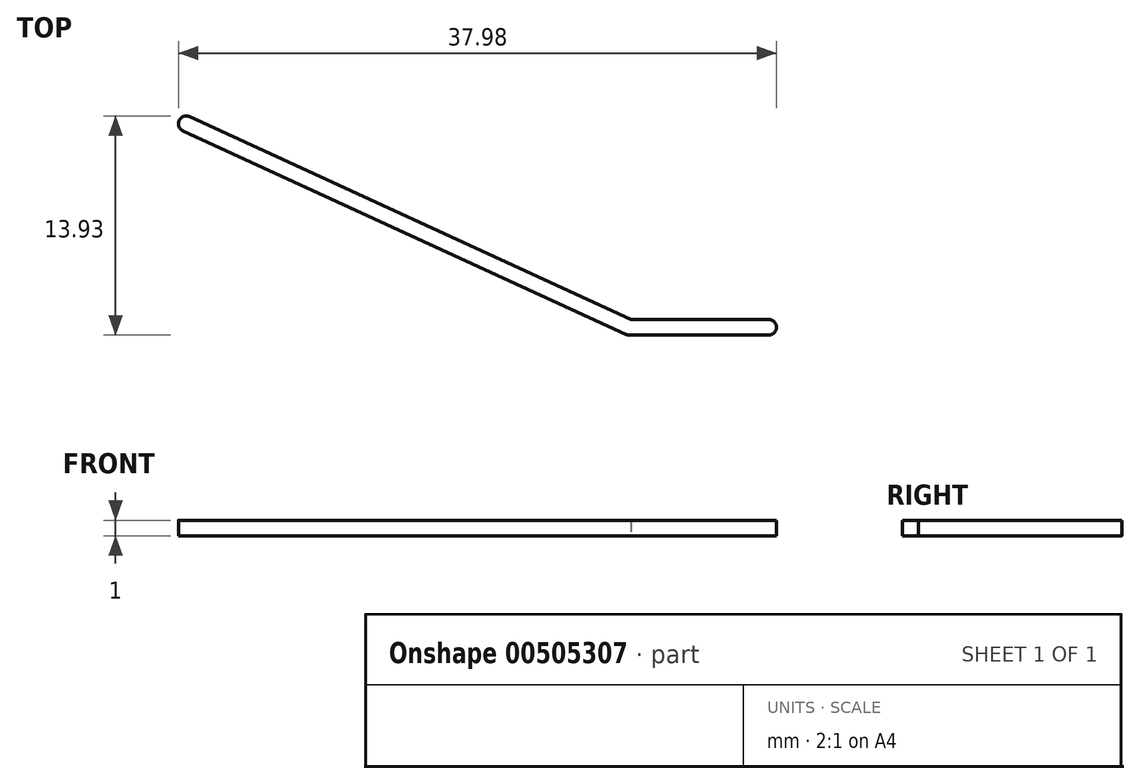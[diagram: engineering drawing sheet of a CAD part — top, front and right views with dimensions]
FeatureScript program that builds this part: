
annotation { "Feature Type Name" : "Feature", "Feature Type Description" : "" }
export const myFeature = defineFeature(function(context is Context, id is Id, definition is map)
    precondition{}
    {
        {
            var Q0;
            Q0=qCreatedBy(makeId("Top.planeOp"),FACE);
            var sketch = newSketch(context, id + "F0", { "sketchPlane" : qUnion([Q0])});
            skLineSegment(sketch, "E0", {"start": v(-63.48, 0) * mm, "end": v(0, 0) * mm});
            skLineSegment(sketch, "E1", {"start": v(0, 0) * mm, "end": v(28.14, -12.93) * mm});
            skLineSegment(sketch, "E2", {"start": v(28.14, -12.93) * mm, "end": v(36.98, -12.93) * mm});
            skLineSegment(sketch, "E3", {"start": v(36.98, -12.93) * mm, "end": v(75.6, 0) * mm});
            skArc(sketch, "E4.0.startCap", {"start": v(-63.48, -0.5) * mm, "mid": v(-63.98, 0) * mm, "end": v(-63.48, 0.5) * mm});
            skArc(sketch, "E4.0.endCap", {"start": v(0, 0.5) * mm, "mid": v(0.5, 0) * mm, "end": v(0, -0.5) * mm});
            skLineSegment(sketch, "E4.0.left", {"start": v(-63.48, 0.5) * mm, "end": v(0, 0.5) * mm});
            skLineSegment(sketch, "E4.0.right", {"start": v(-63.48, -0.5) * mm, "end": v(0, -0.5) * mm});
            skArc(sketch, "E4.1.startCap", {"start": v(-0.2, -0.45) * mm, "mid": v(-0.45, 0.2) * mm, "end": v(0.2, 0.45) * mm});
            skArc(sketch, "E4.1.endCap", {"start": v(28.35, -12.47) * mm, "mid": v(28.6, -13.13) * mm, "end": v(27.93, -13.38) * mm});
            skLineSegment(sketch, "E4.1.left", {"start": v(0.2, 0.45) * mm, "end": v(28.35, -12.47) * mm});
            skLineSegment(sketch, "E4.1.right", {"start": v(-0.2, -0.45) * mm, "end": v(27.93, -13.38) * mm});
            skArc(sketch, "E4.2.startCap", {"start": v(28.14, -13.43) * mm, "mid": v(27.64, -12.93) * mm, "end": v(28.14, -12.43) * mm});
            skArc(sketch, "E4.2.endCap", {"start": v(36.98, -12.43) * mm, "mid": v(37.48, -12.93) * mm, "end": v(36.98, -13.43) * mm});
            skLineSegment(sketch, "E4.2.left", {"start": v(28.14, -12.43) * mm, "end": v(36.98, -12.43) * mm});
            skLineSegment(sketch, "E4.2.right", {"start": v(28.14, -13.43) * mm, "end": v(36.98, -13.43) * mm});
            skArc(sketch, "E4.3.startCap", {"start": v(37.14, -13.4) * mm, "mid": v(36.5, -13.08) * mm, "end": v(36.82, -12.45) * mm});
            skArc(sketch, "E4.3.endCap", {"start": v(75.43, 0.47) * mm, "mid": v(76.07, 0.16) * mm, "end": v(75.75, -0.47) * mm});
            skLineSegment(sketch, "E4.3.left", {"start": v(36.82, -12.45) * mm, "end": v(75.43, 0.47) * mm});
            skLineSegment(sketch, "E4.3.right", {"start": v(37.14, -13.4) * mm, "end": v(75.75, -0.47) * mm});
            skSolve(sketch);
        }
        {
            var Q0;
            {var subQ5=sQuery(id+"F0.wireOp",EDGE,"E4.0.startCap");Q0=makeQuery(id+"F0.imprint","IMPRINT",FACE,{"disambiguationData":[TD([[makeQuery(id+"F0.imprint","IMPRINT",EDGE,{"derivedFrom":subQ5}),-1.0]])]});}
            var Q1;
            {var subQ3=sQuery(id+"F0.wireOp",EDGE,"E1");var subQ5=sQuery(id+"F0.wireOp",EDGE,"E0");var subQ6=makeQuery(id+"F0.imprint","INTERSECT",VERTEX,{"derivedFrom":[subQ5,subQ3]});Q1=makeQuery(id+"F0.imprint","IMPRINT",FACE,{"disambiguationData":[TD([[makeQuery(id+"F0.imprint","IMPRINT",EDGE,{"disambiguationData":[TD([[subQ6,1.0]])],"derivedFrom":subQ5}),1.0]])]});}
            var Q2;
            {var subQ5=sQuery(id+"F0.wireOp",EDGE,"E1");var subQ6=sQuery(id+"F0.wireOp",EDGE,"E0");var subQ7=makeQuery(id+"F0.imprint","INTERSECT",VERTEX,{"derivedFrom":[subQ6,subQ5]});Q2=makeQuery(id+"F0.imprint","IMPRINT",FACE,{"disambiguationData":[TD([[makeQuery(id+"F0.imprint","IMPRINT",EDGE,{"disambiguationData":[TD([[subQ7,1.0]])],"derivedFrom":subQ6}),-1.0]])]});}
            var Q3;
            {var subQ1=sQuery(id+"F0.wireOp",EDGE,"E4.0.endCap");var subQ5=sQuery(id+"F0.wireOp",EDGE,"E1");var subQ6=makeQuery(id+"F0.imprint","INTERSECT",VERTEX,{"derivedFrom":[subQ5,subQ1]});Q3=makeQuery(id+"F0.imprint","IMPRINT",FACE,{"disambiguationData":[TD([[makeQuery(id+"F0.imprint","IMPRINT",EDGE,{"disambiguationData":[TD([[subQ6,-1.0]])],"derivedFrom":subQ5}),-1.0]])]});}
            var Q4;
            {var subQ3=sQuery(id+"F0.wireOp",EDGE,"E1");var subQ6=sQuery(id+"F0.wireOp",EDGE,"E4.0.endCap");var subQ9=makeQuery(id+"F0.imprint","INTERSECT",VERTEX,{"derivedFrom":[subQ3,subQ6]});Q4=makeQuery(id+"F0.imprint","IMPRINT",FACE,{"disambiguationData":[TD([[makeQuery(id+"F0.imprint","IMPRINT",EDGE,{"disambiguationData":[TD([[subQ9,-1.0]])],"derivedFrom":subQ3}),1.0]])]});}
            var Q5;
            {var subQ0=sQuery(id+"F0.wireOp",EDGE,"E2");var subQ1=sQuery(id+"F0.wireOp",EDGE,"E1");var subQ2=makeQuery(id+"F0.imprint","INTERSECT",VERTEX,{"derivedFrom":[subQ1,subQ0]});Q5=makeQuery(id+"F0.imprint","IMPRINT",FACE,{"disambiguationData":[TD([[makeQuery(id+"F0.imprint","IMPRINT",EDGE,{"disambiguationData":[TD([[subQ2,1.0]])],"derivedFrom":subQ1}),-1.0]])]});}
            var Q6;
            {var subQ5=sQuery(id+"F0.wireOp",EDGE,"E2");var subQ9=sQuery(id+"F0.wireOp",EDGE,"E1");var subQ10=makeQuery(id+"F0.imprint","INTERSECT",VERTEX,{"derivedFrom":[subQ9,subQ5]});Q6=makeQuery(id+"F0.imprint","IMPRINT",FACE,{"disambiguationData":[TD([[makeQuery(id+"F0.imprint","IMPRINT",EDGE,{"disambiguationData":[TD([[subQ10,1.0]])],"derivedFrom":subQ9}),1.0]])]});}
            var Q7;
            {var subQ5=sQuery(id+"F0.wireOp",EDGE,"E4.1.endCap");var subQ7=sQuery(id+"F0.wireOp",EDGE,"E2");var subQ8=makeQuery(id+"F0.imprint","INTERSECT",VERTEX,{"derivedFrom":[subQ7,subQ5]});Q7=makeQuery(id+"F0.imprint","IMPRINT",FACE,{"disambiguationData":[TD([[makeQuery(id+"F0.imprint","IMPRINT",EDGE,{"disambiguationData":[TD([[subQ8,-1.0]])],"derivedFrom":subQ7}),1.0]])]});}
            var Q8;
            {var subQ5=sQuery(id+"F0.wireOp",EDGE,"E4.2.right");Q8=makeQuery(id+"F0.imprint","IMPRINT",FACE,{"disambiguationData":[TD([[makeQuery(id+"F0.imprint","IMPRINT",EDGE,{"derivedFrom":subQ5}),1.0]])]});}
            var Q9;
            {var subQ4=sQuery(id+"F0.wireOp",EDGE,"E3");var subQ6=sQuery(id+"F0.wireOp",EDGE,"E2");var subQ7=makeQuery(id+"F0.imprint","INTERSECT",VERTEX,{"derivedFrom":[subQ6,subQ4]});Q9=makeQuery(id+"F0.imprint","IMPRINT",FACE,{"disambiguationData":[TD([[makeQuery(id+"F0.imprint","IMPRINT",EDGE,{"disambiguationData":[TD([[subQ7,1.0]])],"derivedFrom":subQ6}),-1.0]])]});}
            var Q10;
            {var subQ5=sQuery(id+"F0.wireOp",EDGE,"E3");var subQ6=sQuery(id+"F0.wireOp",EDGE,"E2");var subQ7=makeQuery(id+"F0.imprint","INTERSECT",VERTEX,{"derivedFrom":[subQ6,subQ5]});Q10=makeQuery(id+"F0.imprint","IMPRINT",FACE,{"disambiguationData":[TD([[makeQuery(id+"F0.imprint","IMPRINT",EDGE,{"disambiguationData":[TD([[subQ7,1.0]])],"derivedFrom":subQ6}),1.0]])]});}
            var Q11;
            {var subQ0=sQuery(id+"F0.wireOp",EDGE,"E4.3.endCap");Q11=makeQuery(id+"F0.imprint","IMPRINT",FACE,{"disambiguationData":[TD([[makeQuery(id+"F0.imprint","IMPRINT",EDGE,{"derivedFrom":subQ0}),-1.0]])]});}
            extrude(context, id + "F1", {"entities" : qUnion([Q0, Q1, Q2, Q3, Q4, Q5, Q6, Q7, Q8, Q9, Q10, Q11]), "depth" : 1 * mm});
        }
    });
